# Revit family: 3-605 Miro Pendant
name_source: partatom
category: Lighting Fixtures
revit_build: Autodesk Revit 2018 (Build: 20170223_1515(x64)
units: mm (PartAtom-declared; Revit-internal decimal feet)

## family parameters
Always vertical = Yes
Cut with Voids When Loaded = No
Host = Ceiling
Light Source = Yes
OmniClass Number = 23.80.70.11
OmniClass Title = Luminaries for Internal Lighting
Part Type = Normal
Room Calculation Point = No
Round Connector Dimension = Use Diameter
Shared = No

## types (2) — shared parameters
Color Filter = 16777215
Diffusers = Clear Bubble Acrylic
Dimming Lamp Color Temperature Shift = <None>
Lamp = LED Array
Manufacturer = Oxygen - Lighting & Fans
Model = 3-605-xx / Miro Pendant
Photometric Web File = 3-605-24 Miro.ies
References = Ref. 3 = 120 V / Ref. 37 = 277 V
Tilt Angle = 90.00°
URL = www.oxygenlighting.com
Voltage = 120 V
Voltage Input = 120 V or 277 V - 50/60 Hz

## per-type parameters (varying)
| type | Metal Finish | Wattage Comments |
| 3-605-24 / Satin Nickel - Clear Bubble Acrylic | 24 - Satin Nickel | 37 x 2.1 W at 120 V |
| 3-605-40 / Aged Brass - Clear Bubble Acrylic | 40 - Aged Brass | 37 x 3.0 W at 120 V |

## geometry (parser evidence)
native form markers: Blend x4, Sweep x1
no freeform markers — native parametric forms only
